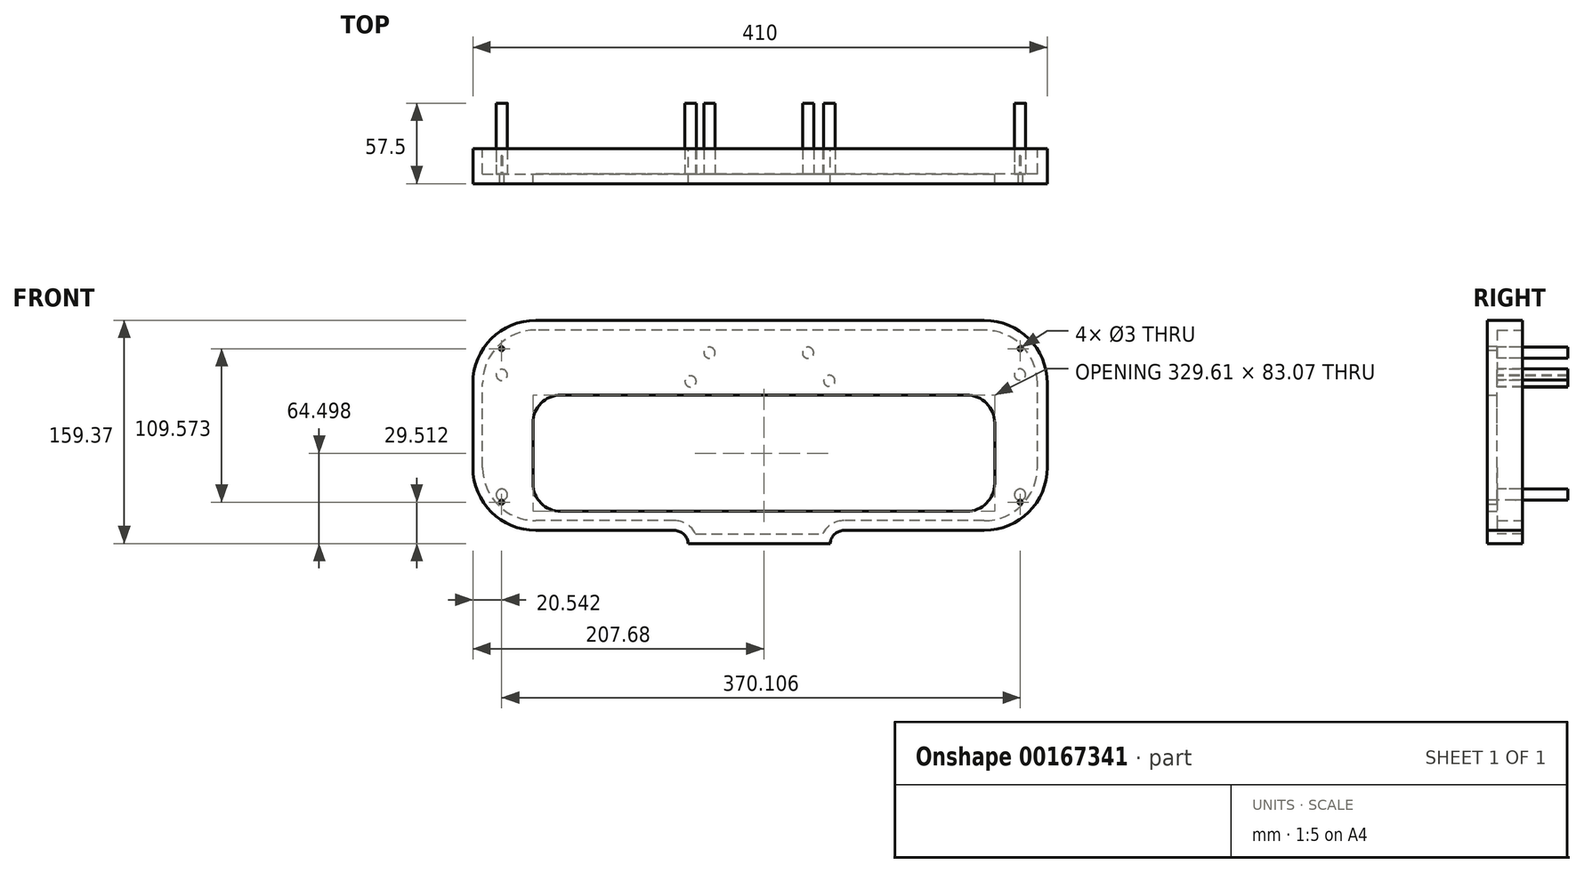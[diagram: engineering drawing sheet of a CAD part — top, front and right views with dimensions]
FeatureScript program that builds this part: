
annotation { "Feature Type Name" : "Feature", "Feature Type Description" : "" }
export const myFeature = defineFeature(function(context is Context, id is Id, definition is map)
    precondition{}
    {
        {
            var Q0;
            Q0=qCreatedBy(makeId("Front.planeOp"),FACE);
            var sketch = newSketch(context, id + "F0", { "sketchPlane" : qUnion([Q0])});
            skLineSegment(sketch, "E0.bottom", {"start": v(205, -75) * mm, "end": v(-205, -75) * mm});
            skLineSegment(sketch, "E0.top", {"start": v(205, 75) * mm, "end": v(-205, 75) * mm});
            skLineSegment(sketch, "E0.left", {"start": v(205, -75) * mm, "end": v(205, 75) * mm});
            skLineSegment(sketch, "E0.right", {"start": v(-205, -75) * mm, "end": v(-205, 75) * mm});
            skSolve(sketch);
        }
        {
            var Q0;
            Q0=qSketchRegion(id+"F0",true);
            extrude(context, id + "F1", {"entities" : qUnion([Q0]), "depth" : 5 * mm, "hasSecondDirection" : true, "secondDirectionOppositeDirection" : true, "secondDirectionDepth" : 20 * mm});
        }
        {
            var Q0;
            Q0=makeQuery(id+"F1.opExtrude","SWEPT_EDGE",EDGE,{"disambiguationData":[OSD([sQuery(id+"F0.wireOp",EDGE,"E0.top"),sQuery(id+"F0.wireOp",EDGE,"E0.right")])]});
            var Q1;
            Q1=makeQuery(id+"F1.opExtrude","SWEPT_EDGE",EDGE,{"disambiguationData":[OSD([sQuery(id+"F0.wireOp",EDGE,"E0.bottom"),sQuery(id+"F0.wireOp",EDGE,"E0.right")])]});
            fillet(context, id + "F2", {"entities" : qUnion([Q0, Q1]), "radius" : 45 * mm, "tangentPropagation" : true, "allowEdgeOverflow" : false});
        }
        {
            var Q0;
            Q0=makeQuery(id+"F1.opExtrude","SWEPT_EDGE",EDGE,{"disambiguationData":[OSD([sQuery(id+"F0.wireOp",EDGE,"E0.top"),sQuery(id+"F0.wireOp",EDGE,"E0.left")])]});
            fillet(context, id + "F3", {"entities" : qUnion([Q0]), "radius" : 45 * mm, "tangentPropagation" : true, "allowEdgeOverflow" : false});
        }
        {
            var Q0;
            Q0=makeQuery(id+"F1.opExtrude","SWEPT_EDGE",EDGE,{"disambiguationData":[OSD([sQuery(id+"F0.wireOp",EDGE,"E0.bottom"),sQuery(id+"F0.wireOp",EDGE,"E0.left")])]});
            fillet(context, id + "F4", {"entities" : qUnion([Q0]), "radius" : 45 * mm, "tangentPropagation" : true, "allowEdgeOverflow" : false});
        }
        {
            var Q0;
            Q0=qCreatedBy(makeId("Front.planeOp"),FACE);
            var sketch = newSketch(context, id + "F5", { "sketchPlane" : qUnion([Q0])});
            skLineSegment(sketch, "E1.bottom", {"start": v(-51.28, -63.48) * mm, "end": v(50, -63.48) * mm});
            skLineSegment(sketch, "E1.top", {"start": v(-51.28, -84.37) * mm, "end": v(50, -84.37) * mm});
            skLineSegment(sketch, "E1.left", {"start": v(-51.28, -63.48) * mm, "end": v(-51.28, -84.37) * mm});
            skLineSegment(sketch, "E1.right", {"start": v(50, -63.48) * mm, "end": v(50, -84.37) * mm});
            skSolve(sketch);
        }
        {
            var Q0;
            Q0=qSketchRegion(id+"F5",true);
            extrude(context, id + "F6", {"entities" : qUnion([Q0]), "operationType" : NewBodyOperationType.ADD, "depth" : 5 * mm, "hasSecondDirection" : true, "secondDirectionOppositeDirection" : true, "secondDirectionDepth" : 20 * mm});
        }
        {
            var Q0;
            Q0=makeQuery(id+"F6.boolean.opBoolean","INTERSECT",EDGE,{"derivedFrom":[makeQuery(id+"F1.opExtrude","SWEPT_FACE",FACE,{"disambiguationData":[OSD([sQuery(id+"F0.wireOp",EDGE,"E0.bottom")])]}),makeQuery(id+"F6.opExtrude","SWEPT_FACE",FACE,{"disambiguationData":[OSD([sQuery(id+"F5.wireOp",EDGE,"E1.left")])]})]});
            fillet(context, id + "F7", {"entities" : qUnion([Q0]), "radius" : 10 * mm, "tangentPropagation" : true, "allowEdgeOverflow" : false});
        }
        {
            var Q0;
            Q0=makeQuery(id+"F6.boolean.opBoolean","INTERSECT",EDGE,{"derivedFrom":[makeQuery(id+"F1.opExtrude","SWEPT_FACE",FACE,{"disambiguationData":[OSD([sQuery(id+"F0.wireOp",EDGE,"E0.bottom")])]}),makeQuery(id+"F6.opExtrude","SWEPT_FACE",FACE,{"disambiguationData":[OSD([sQuery(id+"F5.wireOp",EDGE,"E1.right")])]})]});
            fillet(context, id + "F8", {"entities" : qUnion([Q0]), "radius" : 10 * mm, "tangentPropagation" : true, "allowEdgeOverflow" : false});
        }
        {
            var Q0;
            Q0=makeQuery(id+"F6.boolean.opBoolean","MERGE",FACE,{"derivedFrom":[makeQuery(id+"F1.opExtrude","CAP_FACE",FACE,{"disambiguationData":[OSD([sQuery(id+"F0.wireOp",EDGE,"E0.bottom"),sQuery(id+"F0.wireOp",EDGE,"E0.top"),sQuery(id+"F0.wireOp",EDGE,"E0.left"),sQuery(id+"F0.wireOp",EDGE,"E0.right")])],"isStart":false}),makeQuery(id+"F6.opExtrude","CAP_FACE",FACE,{"disambiguationData":[OSD([sQuery(id+"F5.wireOp",EDGE,"E1.bottom"),sQuery(id+"F5.wireOp",EDGE,"E1.top"),sQuery(id+"F5.wireOp",EDGE,"E1.left"),sQuery(id+"F5.wireOp",EDGE,"E1.right")])],"isStart":false})]});
            cPlane(context, id + "F9", {"entities" : qUnion([Q0]), "cplaneType" : CPlaneType.OFFSET, "offset" : 0 * mm, "width" : 150 * mm, "height" : 150 * mm});
        }
        {
            var Q0;
            Q0=makeQuery(id+"F1.opExtrude","CAP_FACE",FACE,{"disambiguationData":[OSD([sQuery(id+"F0.wireOp",EDGE,"E0.bottom"),sQuery(id+"F0.wireOp",EDGE,"E0.top"),sQuery(id+"F0.wireOp",EDGE,"E0.left"),sQuery(id+"F0.wireOp",EDGE,"E0.right")])],"isStart":true});
            shell(context, id + "F10", {"entities" : qUnion([Q0]), "thickness" : 7 * mm});
        }
        {
            var Q0;
            Q0=makeQuery(id+"F6.boolean.opBoolean","MERGE",FACE,{"derivedFrom":[makeQuery(id+"F1.opExtrude","CAP_FACE",FACE,{"disambiguationData":[OSD([sQuery(id+"F0.wireOp",EDGE,"E0.bottom"),sQuery(id+"F0.wireOp",EDGE,"E0.top"),sQuery(id+"F0.wireOp",EDGE,"E0.left"),sQuery(id+"F0.wireOp",EDGE,"E0.right")])],"isStart":false}),makeQuery(id+"F6.opExtrude","CAP_FACE",FACE,{"disambiguationData":[OSD([sQuery(id+"F5.wireOp",EDGE,"E1.bottom"),sQuery(id+"F5.wireOp",EDGE,"E1.top"),sQuery(id+"F5.wireOp",EDGE,"E1.left"),sQuery(id+"F5.wireOp",EDGE,"E1.right")])],"isStart":false})]});
            cPlane(context, id + "F11", {"entities" : qUnion([Q0]), "cplaneType" : CPlaneType.OFFSET, "offset" : 2 * mm, "oppositeDirection" : true, "width" : 150 * mm, "height" : 150 * mm});
        }
        {
            var Q0;
            Q0=qCreatedBy(id+"F11.planeOp",FACE);
            var sketch = newSketch(context, id + "F12", { "sketchPlane" : qUnion([Q0])});
            skCircle(sketch, "E2", {"center": v(-184.3, 36.01) * mm, "radius": 4 * mm});
            skCircle(sketch, "E3", {"center": v(-184.28, -49.46) * mm, "radius": 4 * mm});
            skCircle(sketch, "E4", {"center": v(-36.07, 51.83) * mm, "radius": 4 * mm});
            skCircle(sketch, "E5", {"center": v(-49.57, 31.39) * mm, "radius": 4 * mm});
            skCircle(sketch, "E6", {"center": v(34.27, 51.83) * mm, "radius": 4 * mm});
            skCircle(sketch, "E7", {"center": v(49.46, 31.76) * mm, "radius": 4 * mm});
            skCircle(sketch, "E8", {"center": v(185.45, 36.26) * mm, "radius": 4 * mm});
            skCircle(sketch, "E9", {"center": v(185.64, -49.46) * mm, "radius": 4 * mm});
            skSolve(sketch);
        }
        {
            var Q0;
            Q0=qSketchRegion(id+"F12",true);
            extrude(context, id + "F13", {"entities" : qUnion([Q0]), "operationType" : NewBodyOperationType.ADD, "oppositeDirection" : true, "depth" : 55.5 * mm});
        }
        {
            var Q0;
            Q0=makeQuery(id+"F0.imprint","IMPRINT",FACE,{"disambiguationData":[TD([[makeQuery(id+"F0.imprint","IMPRINT",EDGE,{"derivedFrom":sQuery(id+"F0.wireOp",EDGE,"E0.bottom")}),-1.0]])]});
            var sketch = newSketch(context, id + "F14", { "sketchPlane" : qUnion([Q0])});
            skLineSegment(sketch, "E10.bottom", {"start": v(167.49, 21.66) * mm, "end": v(-162.13, 21.66) * mm});
            skLineSegment(sketch, "E10.top", {"start": v(167.49, -61.4) * mm, "end": v(-162.13, -61.4) * mm});
            skLineSegment(sketch, "E10.left", {"start": v(167.49, 21.66) * mm, "end": v(167.49, -61.4) * mm});
            skLineSegment(sketch, "E10.right", {"start": v(-162.13, 21.66) * mm, "end": v(-162.13, -61.4) * mm});
            skSolve(sketch);
        }
        {
            var Q0;
            Q0=qSketchRegion(id+"F14",true);
            extrude(context, id + "F15", {"entities" : qUnion([Q0]), "operationType" : NewBodyOperationType.REMOVE, "depth" : 25 * mm, "hasSecondDirection" : true, "secondDirectionOppositeDirection" : true, "secondDirectionDepth" : 25 * mm});
        }
        {
            var Q0;
            Q0=makeQuery(id+"F15.boolean.opBoolean","COPY",EDGE,{"derivedFrom":makeQuery(id+"F15.opExtrude","SWEPT_EDGE",EDGE,{"disambiguationData":[OSD([sQuery(id+"F14.wireOp",EDGE,"E10.bottom"),sQuery(id+"F14.wireOp",EDGE,"E10.right")])]})});
            var Q1;
            Q1=makeQuery(id+"F15.boolean.opBoolean","COPY",EDGE,{"derivedFrom":makeQuery(id+"F15.opExtrude","SWEPT_EDGE",EDGE,{"disambiguationData":[OSD([sQuery(id+"F14.wireOp",EDGE,"E10.bottom"),sQuery(id+"F14.wireOp",EDGE,"E10.left")])]})});
            var Q2;
            Q2=makeQuery(id+"F15.boolean.opBoolean","COPY",EDGE,{"derivedFrom":makeQuery(id+"F15.opExtrude","SWEPT_EDGE",EDGE,{"disambiguationData":[OSD([sQuery(id+"F14.wireOp",EDGE,"E10.top"),sQuery(id+"F14.wireOp",EDGE,"E10.left")])]})});
            var Q3;
            Q3=makeQuery(id+"F15.boolean.opBoolean","COPY",EDGE,{"derivedFrom":makeQuery(id+"F15.opExtrude","SWEPT_EDGE",EDGE,{"disambiguationData":[OSD([sQuery(id+"F14.wireOp",EDGE,"E10.top"),sQuery(id+"F14.wireOp",EDGE,"E10.right")])]})});
            fillet(context, id + "F16", {"entities" : qUnion([Q0, Q1, Q2, Q3]), "radius" : 20 * mm, "tangentPropagation" : true, "allowEdgeOverflow" : false});
        }
        {
            var Q0;
            Q0=makeQuery(id+"F13.opExtrude","CAP_FACE",FACE,{"disambiguationData":[OSD([sQuery(id+"F12.wireOp",EDGE,"E8")])],"isStart":false});
            cPlane(context, id + "F17", {"entities" : qUnion([Q0]), "cplaneType" : CPlaneType.OFFSET, "offset" : 0 * mm, "width" : 150 * mm, "height" : 150 * mm});
        }
        {
            var Q0;
            Q0=makeQuery(id+"F6.boolean.opBoolean","MERGE",FACE,{"derivedFrom":[makeQuery(id+"F1.opExtrude","CAP_FACE",FACE,{"disambiguationData":[OSD([sQuery(id+"F0.wireOp",EDGE,"E0.bottom"),sQuery(id+"F0.wireOp",EDGE,"E0.top"),sQuery(id+"F0.wireOp",EDGE,"E0.left"),sQuery(id+"F0.wireOp",EDGE,"E0.right")])],"isStart":false}),makeQuery(id+"F6.opExtrude","CAP_FACE",FACE,{"disambiguationData":[OSD([sQuery(id+"F5.wireOp",EDGE,"E1.bottom"),sQuery(id+"F5.wireOp",EDGE,"E1.top"),sQuery(id+"F5.wireOp",EDGE,"E1.left"),sQuery(id+"F5.wireOp",EDGE,"E1.right")])],"isStart":false})]});
            cPlane(context, id + "F18", {"entities" : qUnion([Q0]), "cplaneType" : CPlaneType.OFFSET, "offset" : 0 * mm, "width" : 150 * mm, "height" : 150 * mm});
        }
        {
            var Q0;
            Q0=qCreatedBy(id+"F18.planeOp",FACE);
            var sketch = newSketch(context, id + "F19", { "sketchPlane" : qUnion([Q0])});
            skLineSegment(sketch, "E11.bottom", {"start": v(-184.46, 54.71) * mm, "end": v(185.65, 54.71) * mm, "construction": true});
            skLineSegment(sketch, "E11.top", {"start": v(-184.46, -54.86) * mm, "end": v(185.65, -54.86) * mm, "construction": true});
            skLineSegment(sketch, "E11.left", {"start": v(-184.46, 54.71) * mm, "end": v(-184.46, -54.86) * mm, "construction": true});
            skLineSegment(sketch, "E11.right", {"start": v(185.65, 54.71) * mm, "end": v(185.65, -54.86) * mm, "construction": true});
            skPoint(sketch, "E12", {"position": v(-184.46, 54.71) * mm});
            skPoint(sketch, "E13", {"position": v(-184.46, -54.86) * mm});
            skPoint(sketch, "E14", {"position": v(185.65, -54.86) * mm});
            skPoint(sketch, "E15", {"position": v(185.65, 54.71) * mm});
            skSolve(sketch);
        }
        {
            var Q0;
            Q0=sQuery(id+"F19.wireOp",VERTEX,"E12");
            var Q1;
            Q1=sQuery(id+"F19.wireOp",VERTEX,"E13");
            var Q2;
            Q2=sQuery(id+"F19.wireOp",VERTEX,"E14");
            var Q3;
            Q3=sQuery(id+"F19.wireOp",VERTEX,"E15");
            var Q4;
            Q4=makeQuery(id+"F1.opExtrude","SWEPT_BODY",BODY,{"disambiguationData":[OSD([sQuery(id+"F0.wireOp",EDGE,"E0.bottom"),sQuery(id+"F0.wireOp",EDGE,"E0.top"),sQuery(id+"F0.wireOp",EDGE,"E0.left"),sQuery(id+"F0.wireOp",EDGE,"E0.right")])]});
            hole(context, id + "F20", {"style" : HoleStyle.SIMPLE, "endStyle" : HoleEndStyle.BLIND, "holeDiameter" : 3 * mm, "holeDepth" : 20 * mm, "locations" : qUnion([Q0, Q1, Q2, Q3]), "scope" : qUnion([Q4])});
        }
    });
